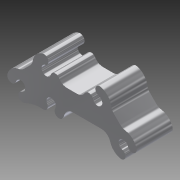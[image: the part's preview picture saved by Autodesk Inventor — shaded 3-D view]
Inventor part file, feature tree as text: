
AUTODESK INVENTOR PART (.ipt)
format: ipt  version: 2014 (Build 180170000, 170)  size: 151,040 bytes
history: native  units: in
note: dims shown in document units (in); Inventor stores cm internally (conversion verified against a paired STEP export)
features: extrude x1, sketch x1
ambient origin geometry x8: Origin, YZ Plane, XZ Plane, XY Plane, X Axis, Y Axis, Z Axis, Center Point
bodies: Solid1 (feature_tree)
feature tree (2):
  extrude  "Extrusion1"  [1 undecoded]
  sketch  "Sketch1"  dims[d0=0.995in d1=0.0in]
note: 1 required parameter value undecoded (feature->parameter linkage not recoverable at this tier; creation-order binding heuristic only, values carry confidence <= 0.55)
